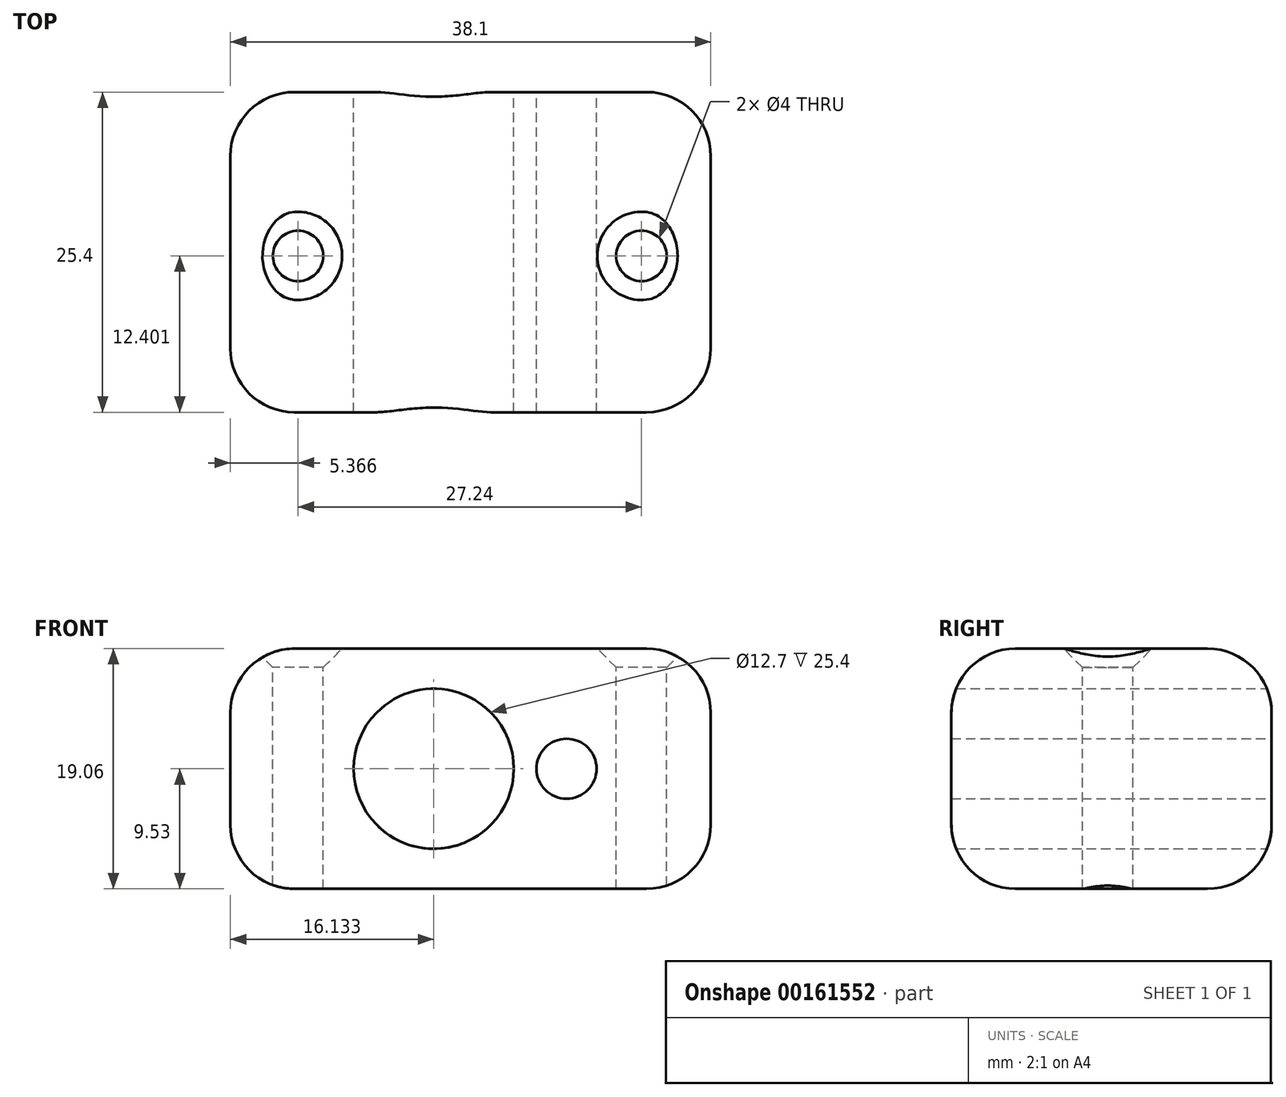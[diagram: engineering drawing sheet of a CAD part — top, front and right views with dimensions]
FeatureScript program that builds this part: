
annotation { "Feature Type Name" : "Feature", "Feature Type Description" : "" }
export const myFeature = defineFeature(function(context is Context, id is Id, definition is map)
    precondition{}
    {
        {
            var Q0;
            Q0=qCreatedBy(makeId("Front.planeOp"),FACE);
            var sketch = newSketch(context, id + "F0", { "sketchPlane" : qUnion([Q0])});
            skLineSegment(sketch, "E0.bottom", {"start": v(-19.05, -9.53) * mm, "end": v(19.05, -9.53) * mm});
            skLineSegment(sketch, "E0.top", {"start": v(-19.05, 9.53) * mm, "end": v(19.05, 9.53) * mm});
            skLineSegment(sketch, "E0.left", {"start": v(-19.05, -9.53) * mm, "end": v(-19.05, 9.52) * mm});
            skLineSegment(sketch, "E0.right", {"start": v(19.05, -9.53) * mm, "end": v(19.05, 9.52) * mm});
            skPoint(sketch, "E0.middle", {"position": v(0, 0) * mm});
            skPoint(sketch, "E1", {"position": v(-2.92, 0) * mm});
            skPoint(sketch, "E2", {"position": v(7.61, 0) * mm});
            skSolve(sketch);
        }
        {
            var Q0;
            Q0 = qSketchRegion(id + "F0", true);
            extrude(context, id + "F1", {"entities" : qUnion([Q0]), "depth" : 25.4 * mm});
        }
        {
            var Q0;
            Q0=sQuery(id+"F0.wireOp",VERTEX,"E1");
            var Q1;
            Q1=makeQuery(id+"F1.opExtrude","SWEPT_BODY",BODY,{"disambiguationData":[OSD([sQuery(id+"F0.wireOp",EDGE,"E0.bottom"),sQuery(id+"F0.wireOp",EDGE,"E0.top"),sQuery(id+"F0.wireOp",EDGE,"E0.left"),sQuery(id+"F0.wireOp",EDGE,"E0.right")])]});
            hole(context, id + "F2", {"style" : HoleStyle.SIMPLE, "endStyle" : HoleEndStyle.THROUGH, "oppositeDirection" : true, "holeDiameter" : 12.7 * mm, "startFromSketch" : true, "locations" : qUnion([Q0]), "scope" : qUnion([Q1]), "isTappedThrough" : true});
        }
        {
            var Q0;
            Q0=sQuery(id+"F0.wireOp",VERTEX,"E2");
            var Q1;
            Q1=makeQuery(id+"F1.opExtrude","SWEPT_BODY",BODY,{"disambiguationData":[OSD([sQuery(id+"F0.wireOp",EDGE,"E0.bottom"),sQuery(id+"F0.wireOp",EDGE,"E0.top"),sQuery(id+"F0.wireOp",EDGE,"E0.left"),sQuery(id+"F0.wireOp",EDGE,"E0.right")])]});
            hole(context, id + "F3", {"style" : HoleStyle.SIMPLE, "endStyle" : HoleEndStyle.THROUGH, "oppositeDirection" : true, "holeDiameter" : 4.76 * mm, "startFromSketch" : true, "locations" : qUnion([Q0]), "scope" : qUnion([Q1]), "isTappedThrough" : true});
        }
        {
            var Q0;
            Q0=makeQuery(id+"F1.opExtrude","SWEPT_FACE",FACE,{"disambiguationData":[OSD([sQuery(id+"F0.wireOp",EDGE,"E0.top")])]});
            var sketch = newSketch(context, id + "F4", { "sketchPlane" : qUnion([Q0])});
            skPoint(sketch, "E3", {"position": v(-13.68, -13) * mm});
            skPoint(sketch, "E4", {"position": v(13.56, -13) * mm});
            skSolve(sketch);
        }
        {
            var Q0;
            Q0=sQuery(id+"F4.wireOp",VERTEX,"E3");
            var Q1;
            Q1=sQuery(id+"F4.wireOp",VERTEX,"E4");
            var Q2;
            Q2=makeQuery(id+"F1.opExtrude","SWEPT_BODY",BODY,{"disambiguationData":[OSD([sQuery(id+"F0.wireOp",EDGE,"E0.bottom"),sQuery(id+"F0.wireOp",EDGE,"E0.top"),sQuery(id+"F0.wireOp",EDGE,"E0.left"),sQuery(id+"F0.wireOp",EDGE,"E0.right")])]});
            hole(context, id + "F5", {"style" : HoleStyle.C_SINK, "endStyle" : HoleEndStyle.THROUGH, "holeDiameter" : 4 * mm, "cSinkDiameter" : 7 * mm, "cSinkAngle" : 90 * degree, "startFromSketch" : true, "locations" : qUnion([Q0, Q1]), "scope" : qUnion([Q2]), "isTappedThrough" : true});
        }
        {
            var Q0;
            Q0=makeQuery(id+"F1.opExtrude","CAP_EDGE",EDGE,{"disambiguationData":[OSD([sQuery(id+"F0.wireOp",EDGE,"E0.top")])],"isStart":true});
            var Q1;
            Q1=makeQuery(id+"F1.opExtrude","CAP_EDGE",EDGE,{"disambiguationData":[OSD([sQuery(id+"F0.wireOp",EDGE,"E0.top")])],"isStart":false});
            var Q2;
            Q2=makeQuery(id+"F1.opExtrude","CAP_EDGE",EDGE,{"disambiguationData":[OSD([sQuery(id+"F0.wireOp",EDGE,"E0.bottom")])],"isStart":false});
            var Q3;
            Q3=makeQuery(id+"F1.opExtrude","CAP_EDGE",EDGE,{"disambiguationData":[OSD([sQuery(id+"F0.wireOp",EDGE,"E0.bottom")])],"isStart":true});
            var Q4;
            Q4=makeQuery(id+"F1.opExtrude","SWEPT_FACE",FACE,{"disambiguationData":[OSD([sQuery(id+"F0.wireOp",EDGE,"E0.right")])]});
            var Q5;
            Q5=makeQuery(id+"F1.opExtrude","SWEPT_FACE",FACE,{"disambiguationData":[OSD([sQuery(id+"F0.wireOp",EDGE,"E0.left")])]});
            fillet(context, id + "F6", {"entities" : qUnion([Q0, Q1, Q2, Q3, Q4, Q5]), "radius" : 5.08 * mm, "tangentPropagation" : true, "allowEdgeOverflow" : false});
        }
    });
